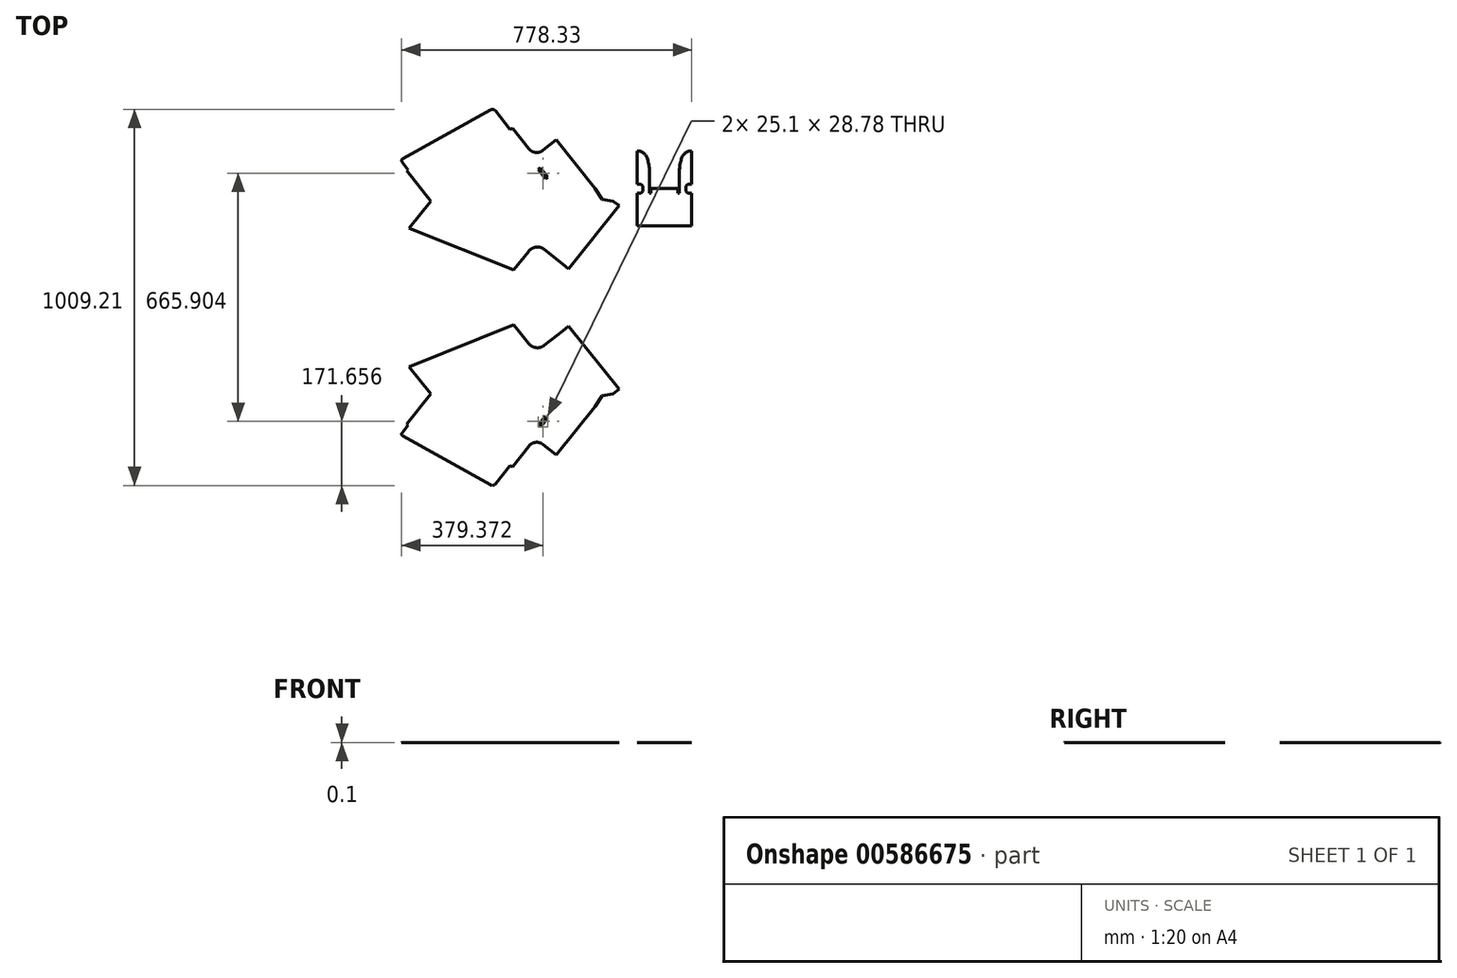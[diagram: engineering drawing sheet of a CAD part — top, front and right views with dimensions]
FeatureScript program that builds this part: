
annotation { "Feature Type Name" : "Feature", "Feature Type Description" : "" }
export const myFeature = defineFeature(function(context is Context, id is Id, definition is map)
    precondition{}
    {
        {
            var Q0;
            Q0=qCreatedBy(makeId("Top.planeOp"),FACE);
            var sketch = newSketch(context, id + "F0", { "sketchPlane" : qUnion([Q0])});
            skLineSegment(sketch, "E0", {"start": v(254.37, -112.24) * mm, "end": v(254.37, 88.8) * mm});
            skLineSegment(sketch, "E1", {"start": v(221.35, -24.07) * mm, "end": v(221.35, 30.01) * mm});
            skLineSegment(sketch, "E2", {"start": v(221.35, -24.07) * mm, "end": v(221.35, -112.24) * mm, "construction": true});
            skLineSegment(sketch, "E3", {"start": v(225.7, -112.24) * mm, "end": v(225.7, -24.07) * mm, "construction": true});
            skLineSegment(sketch, "E4", {"start": v(225.7, -24.07) * mm, "end": v(221.35, -24.07) * mm, "construction": true});
            skLineSegment(sketch, "E5", {"start": v(254.37, -0.56) * mm, "end": v(243.82, -0.56) * mm});
            skLineSegment(sketch, "E6", {"start": v(243.82, -0.56) * mm, "end": v(239.01, -5.44) * mm});
            skLineSegment(sketch, "E7", {"start": v(239.01, -5.44) * mm, "end": v(239.01, -19.29) * mm});
            skLineSegment(sketch, "E8", {"start": v(239.01, -19.29) * mm, "end": v(243.8, -24.07) * mm});
            skLineSegment(sketch, "E9", {"start": v(243.8, -24.07) * mm, "end": v(254.37, -24.07) * mm});
            skLineSegment(sketch, "E10", {"start": v(254.37, -112.24) * mm, "end": v(225.7, -112.24) * mm});
            skLineSegment(sketch, "E11", {"start": v(225.7, -112.24) * mm, "end": v(221.35, -112.24) * mm});
            skPoint(sketch, "E12.orphan", {"position": v(180.8, -112.24) * mm});
            skFitSpline(sketch, "E13", {"points": [v(254.37, 88.8) * mm, v(238.23, 84.23) * mm, v(227.74, 70.37) * mm, v(221.35, 30.01) * mm], "startDerivative": vector(-68.77, 3.22) * mm, "endDerivative": vector(2.4, -103.68) * mm});
            skLineSegment(sketch, "E14.MirrorCS", {"start": v(136.44, -112.24) * mm, "end": v(140.8, -112.24) * mm});
            skLineSegment(sketch, "E15.MirrorCS", {"start": v(136.44, -24.07) * mm, "end": v(140.8, -24.07) * mm, "construction": true});
            skLineSegment(sketch, "E16.MirrorCS", {"start": v(123.13, -19.29) * mm, "end": v(118.34, -24.07) * mm});
            skLineSegment(sketch, "E17.MirrorCS", {"start": v(118.33, -0.56) * mm, "end": v(123.13, -5.44) * mm});
            skLineSegment(sketch, "E18.MirrorCS", {"start": v(107.77, -0.56) * mm, "end": v(118.33, -0.56) * mm});
            skLineSegment(sketch, "E19.MirrorCS", {"start": v(118.34, -24.07) * mm, "end": v(107.77, -24.07) * mm});
            skLineSegment(sketch, "E20.MirrorCS", {"start": v(107.77, -112.24) * mm, "end": v(136.44, -112.24) * mm});
            skLineSegment(sketch, "E21.MirrorCS", {"start": v(107.77, -112.24) * mm, "end": v(107.77, 88.8) * mm});
            skLineSegment(sketch, "E22.MirrorCS", {"start": v(136.44, -112.24) * mm, "end": v(136.44, -24.07) * mm, "construction": true});
            skLineSegment(sketch, "E23.MirrorCS", {"start": v(123.13, -5.44) * mm, "end": v(123.13, -19.29) * mm});
            skFitSpline(sketch, "E24.MirrorCS", {"points": [v(107.77, 88.8) * mm, v(123.92, 84.23) * mm, v(134.4, 70.37) * mm, v(140.8, 30.01) * mm], "startDerivative": vector(68.77, 3.22) * mm, "endDerivative": vector(-2.4, -103.68) * mm});
            skLineSegment(sketch, "E25.MirrorCS", {"start": v(140.8, -24.07) * mm, "end": v(140.8, 30.01) * mm});
            skLineSegment(sketch, "E26.MirrorCS", {"start": v(140.8, -24.07) * mm, "end": v(140.8, -112.24) * mm, "construction": true});
            skPoint(sketch, "E27.start.orphan", {"position": v(201.07, -112.24) * mm});
            skLineSegment(sketch, "E28", {"start": v(140.8, -112.24) * mm, "end": v(221.35, -112.24) * mm});
            skLineSegment(sketch, "E29", {"start": v(221.35, -24.07) * mm, "end": v(217.04, -24.07) * mm});
            skLineSegment(sketch, "E30", {"start": v(217.04, -24.07) * mm, "end": v(217.04, -12.27) * mm});
            skLineSegment(sketch, "E31", {"start": v(217.04, -12.27) * mm, "end": v(181.07, -12.27) * mm});
            skLineSegment(sketch, "E32", {"start": v(181.07, -12.27) * mm, "end": v(145.18, -12.27) * mm});
            skLineSegment(sketch, "E33", {"start": v(145.18, -12.27) * mm, "end": v(145.18, -24.07) * mm});
            skLineSegment(sketch, "E34", {"start": v(145.18, -24.07) * mm, "end": v(140.8, -24.07) * mm});
            skLineSegment(sketch, "E35", {"start": v(145.18, -24.07) * mm, "end": v(217.04, -24.07) * mm, "construction": true});
            skLineSegment(sketch, "E36.MirrorCS", {"start": v(59.36, -57.97) * mm, "end": v(43.76, -45.46) * mm});
            skLineSegment(sketch, "E37.MirrorCS", {"start": v(-5.49, -11.54) * mm, "end": v(14.37, -40.75) * mm});
            skLineSegment(sketch, "E38.MirrorCS", {"start": v(-76.36, -227.13) * mm, "end": v(-91.96, -214.62) * mm});
            skLineSegment(sketch, "E39.MirrorCS", {"start": v(-233.12, 147.2) * mm, "end": v(-226.32, 149.8) * mm});
            skLineSegment(sketch, "E40.MirrorCS", {"start": v(14.37, -40.75) * mm, "end": v(43.76, -45.46) * mm});
            skLineSegment(sketch, "E41.MirrorCS", {"start": v(-511.04, 36) * mm, "end": v(-506.06, 37.96) * mm});
            skLineSegment(sketch, "E42.MirrorCS", {"start": v(-132.04, 19.18) * mm, "end": v(-138.06, 14.4) * mm});
            skLineSegment(sketch, "E43.MirrorCS", {"start": v(-157.14, 38.42) * mm, "end": v(-151.15, 43.18) * mm});
            skArc(sketch, "E44.MirrorCS", {"start": v(-286.33, 199) * mm, "mid": v(-278.7, 200.23) * mm, "end": v(-272.08, 196.22) * mm});
            skLineSegment(sketch, "E45.MirrorCS", {"start": v(-151.15, 43.18) * mm, "end": v(-132.04, 19.18) * mm});
            skLineSegment(sketch, "E46.MirrorCS", {"start": v(-506.06, 37.96) * mm, "end": v(-522.56, 58.67) * mm});
            skArc(sketch, "E47.MirrorCS", {"start": v(-522.56, 58.67) * mm, "mid": v(-523.84, 63.89) * mm, "end": v(-520.69, 68.25) * mm});
            skLineSegment(sketch, "E48.MirrorCS", {"start": v(-138.06, 14.4) * mm, "end": v(-157.14, 38.42) * mm});
            skLineSegment(sketch, "E49.MirrorCS", {"start": v(-482.52, 0.13) * mm, "end": v(-58.86, 55.82) * mm, "construction": true});
            skLineSegment(sketch, "E50.MirrorCS", {"start": v(-446.24, -45.46) * mm, "end": v(-511.04, 36) * mm});
            skLineSegment(sketch, "E51.MirrorCS", {"start": v(-91.96, -214.62) * mm, "end": v(-140.69, -175.66) * mm});
            skArc(sketch, "E52.MirrorCS", {"start": v(-144.6, 90.65) * mm, "mid": v(-164.65, 84.9) * mm, "end": v(-182.9, 95.04) * mm});
            skLineSegment(sketch, "E53.MirrorCS", {"start": v(-144.6, 90.65) * mm, "end": v(-108.97, 119.07) * mm});
            skLineSegment(sketch, "E54.MirrorCS", {"start": v(-226.32, 149.8) * mm, "end": v(-182.9, 95.04) * mm});
            skLineSegment(sketch, "E55.MirrorCS", {"start": v(-233.12, 147.2) * mm, "end": v(-506.06, 37.96) * mm, "construction": true});
            skLineSegment(sketch, "E56.MirrorCS", {"start": v(-183.54, -180.54) * mm, "end": v(-223.37, -230.83) * mm});
            skLineSegment(sketch, "E57.MirrorCS", {"start": v(-520.69, 68.25) * mm, "end": v(-286.33, 199) * mm});
            skLineSegment(sketch, "E58.MirrorCS", {"start": v(-223.37, -230.83) * mm, "end": v(-504.18, -117.98) * mm});
            skLineSegment(sketch, "E59.MirrorCS", {"start": v(-459.2, -29.18) * mm, "end": v(-5.49, -11.54) * mm, "construction": true});
            skLineSegment(sketch, "E60.MirrorCS", {"start": v(43.76, -45.46) * mm, "end": v(-91.96, -214.62) * mm});
            skLineSegment(sketch, "E61.MirrorCS", {"start": v(-108.97, 119.07) * mm, "end": v(-5.49, -11.54) * mm});
            skLineSegment(sketch, "E62.MirrorCS", {"start": v(-446.24, -45.46) * mm, "end": v(43.76, -45.46) * mm, "construction": true});
            skArc(sketch, "E63.MirrorCS", {"start": v(-183.54, -180.54) * mm, "mid": v(-163.13, -169.2) * mm, "end": v(-140.69, -175.66) * mm});
            skLineSegment(sketch, "E64.MirrorCS", {"start": v(-32.72, 22.83) * mm, "end": v(-472.16, -12.89) * mm, "construction": true});
            skLineSegment(sketch, "E65.MirrorCS", {"start": v(-509.12, 41.8) * mm, "end": v(-236.17, 151.03) * mm, "construction": true});
            skLineSegment(sketch, "E66.MirrorCS", {"start": v(40, -50.14) * mm, "end": v(-449.98, -50.15) * mm, "construction": true});
            skLineSegment(sketch, "E67.MirrorCS", {"start": v(59.36, -57.97) * mm, "end": v(-76.36, -227.13) * mm});
            skLineSegment(sketch, "E68.MirrorCS", {"start": v(14.37, -40.75) * mm, "end": v(-449.98, -40.76) * mm, "construction": true});
            skLineSegment(sketch, "E69.MirrorCS", {"start": v(-504.18, -117.98) * mm, "end": v(-446.24, -45.46) * mm});
            skLineSegment(sketch, "E70.MirrorCS", {"start": v(-272.08, 196.22) * mm, "end": v(-233.12, 147.2) * mm});
            skLineSegment(sketch, "E71", {"start": v(-557.03, -304.16) * mm, "end": v(110.66, -304.16) * mm, "construction": true});
            skLineSegment(sketch, "E72.MirrorCS", {"start": v(59.36, -550.35) * mm, "end": v(43.76, -562.86) * mm});
            skLineSegment(sketch, "E73.MirrorCS", {"start": v(-157.14, -646.74) * mm, "end": v(-151.15, -651.5) * mm});
            skLineSegment(sketch, "E74.MirrorCS", {"start": v(-511.04, -644.31) * mm, "end": v(-506.06, -646.28) * mm});
            skLineSegment(sketch, "E75.MirrorCS", {"start": v(-151.15, -651.5) * mm, "end": v(-132.04, -627.5) * mm});
            skLineSegment(sketch, "E76.MirrorCS", {"start": v(-506.06, -646.28) * mm, "end": v(-522.56, -666.99) * mm});
            skLineSegment(sketch, "E77.MirrorCS", {"start": v(14.37, -567.57) * mm, "end": v(43.76, -562.86) * mm});
            skLineSegment(sketch, "E78.MirrorCS", {"start": v(-5.49, -596.79) * mm, "end": v(14.37, -567.57) * mm});
            skLineSegment(sketch, "E79.MirrorCS", {"start": v(-233.12, -755.51) * mm, "end": v(-226.32, -758.13) * mm});
            skLineSegment(sketch, "E80.MirrorCS", {"start": v(-76.36, -381.2) * mm, "end": v(-91.96, -393.7) * mm});
            skLineSegment(sketch, "E81.MirrorCS", {"start": v(-91.96, -393.7) * mm, "end": v(-140.69, -432.66) * mm});
            skLineSegment(sketch, "E82.MirrorCS", {"start": v(-132.04, -627.5) * mm, "end": v(-138.06, -622.72) * mm});
            skArc(sketch, "E83.MirrorCS", {"start": v(-144.6, -698.98) * mm, "mid": v(-164.65, -693.21) * mm, "end": v(-182.9, -703.36) * mm});
            skLineSegment(sketch, "E84.MirrorCS", {"start": v(-144.6, -698.98) * mm, "end": v(-108.97, -727.4) * mm});
            skLineSegment(sketch, "E85.MirrorCS", {"start": v(-138.06, -622.72) * mm, "end": v(-157.14, -646.74) * mm});
            skArc(sketch, "E86.MirrorCS", {"start": v(-183.54, -427.78) * mm, "mid": v(-163.13, -439.13) * mm, "end": v(-140.69, -432.66) * mm});
            skArc(sketch, "E87.MirrorCS", {"start": v(-522.56, -666.99) * mm, "mid": v(-523.84, -672.21) * mm, "end": v(-520.69, -676.57) * mm});
            skArc(sketch, "E88.MirrorCS", {"start": v(-286.33, -807.32) * mm, "mid": v(-278.7, -808.56) * mm, "end": v(-272.08, -804.54) * mm});
            skLineSegment(sketch, "E89.MirrorCS", {"start": v(-446.24, -562.86) * mm, "end": v(-511.04, -644.31) * mm});
            skLineSegment(sketch, "E90.MirrorCS", {"start": v(-272.08, -804.54) * mm, "end": v(-233.12, -755.51) * mm});
            skLineSegment(sketch, "E91.MirrorCS", {"start": v(-446.24, -562.86) * mm, "end": v(43.76, -562.86) * mm, "construction": true});
            skLineSegment(sketch, "E92.MirrorCS", {"start": v(14.37, -567.57) * mm, "end": v(-449.98, -567.56) * mm, "construction": true});
            skLineSegment(sketch, "E93.MirrorCS", {"start": v(-459.2, -579.15) * mm, "end": v(-5.49, -596.79) * mm, "construction": true});
            skLineSegment(sketch, "E94.MirrorCS", {"start": v(59.36, -550.35) * mm, "end": v(-76.36, -381.2) * mm});
            skLineSegment(sketch, "E95.MirrorCS", {"start": v(-223.37, -377.5) * mm, "end": v(-504.18, -490.35) * mm});
            skLineSegment(sketch, "E96.MirrorCS", {"start": v(40, -558.18) * mm, "end": v(-449.98, -558.17) * mm, "construction": true});
            skLineSegment(sketch, "E97.MirrorCS", {"start": v(-520.69, -676.57) * mm, "end": v(-286.33, -807.32) * mm});
            skLineSegment(sketch, "E98.MirrorCS", {"start": v(-482.52, -608.46) * mm, "end": v(-58.86, -664.14) * mm, "construction": true});
            skLineSegment(sketch, "E99.MirrorCS", {"start": v(-183.54, -427.78) * mm, "end": v(-223.37, -377.5) * mm});
            skLineSegment(sketch, "E100.MirrorCS", {"start": v(-509.12, -650.12) * mm, "end": v(-236.17, -759.35) * mm, "construction": true});
            skLineSegment(sketch, "E101.MirrorCS", {"start": v(-233.12, -755.51) * mm, "end": v(-506.06, -646.28) * mm, "construction": true});
            skLineSegment(sketch, "E102.MirrorCS", {"start": v(-108.97, -727.4) * mm, "end": v(-5.49, -596.79) * mm});
            skLineSegment(sketch, "E103.MirrorCS", {"start": v(-226.32, -758.13) * mm, "end": v(-182.9, -703.36) * mm});
            skLineSegment(sketch, "E104.MirrorCS", {"start": v(43.76, -562.86) * mm, "end": v(-91.96, -393.7) * mm});
            skLineSegment(sketch, "E105.MirrorCS", {"start": v(-504.18, -490.35) * mm, "end": v(-446.24, -562.86) * mm});
            skLineSegment(sketch, "E106.MirrorCS", {"start": v(-32.72, -631.15) * mm, "end": v(-472.16, -595.44) * mm, "construction": true});
            skSolve(sketch);
        }
        {
            var Q0;
            Q0=makeQuery(id+"F0.imprint","IMPRINT",FACE,{"disambiguationData":[TD([[makeQuery(id+"F0.imprint","IMPRINT",EDGE,{"derivedFrom":sQuery(id+"F0.wireOp",EDGE,"E1")}),-1.0]])]});
            var Q1;
            Q1=makeQuery(id+"F0.imprint","IMPRINT",FACE,{"disambiguationData":[TD([[makeQuery(id+"F0.imprint","IMPRINT",EDGE,{"derivedFrom":sQuery(id+"F0.wireOp",EDGE,"E37.MirrorCS")}),-1.0]])]});
            var Q2;
            Q2=makeQuery(id+"F0.imprint","IMPRINT",FACE,{"disambiguationData":[TD([[makeQuery(id+"F0.imprint","IMPRINT",EDGE,{"derivedFrom":sQuery(id+"F0.wireOp",EDGE,"E36.MirrorCS")}),1.0]])]});
            var Q3;
            Q3=makeQuery(id+"F0.imprint","IMPRINT",FACE,{"disambiguationData":[TD([[makeQuery(id+"F0.imprint","IMPRINT",EDGE,{"derivedFrom":sQuery(id+"F0.wireOp",EDGE,"E73.MirrorCS")}),-1.0]])]});
            var Q4;
            Q4=makeQuery(id+"F0.imprint","IMPRINT",FACE,{"disambiguationData":[TD([[makeQuery(id+"F0.imprint","IMPRINT",EDGE,{"derivedFrom":sQuery(id+"F0.wireOp",EDGE,"E72.MirrorCS")}),-1.0]])]});
            extrude(context, id + "F1", {"entities" : qUnion([Q0, Q1, Q2, Q3, Q4]), "oppositeDirection" : true, "depth" : .1 * mm, "offsetDistance" : 25 * mm});
        }
    });
